# Revit family: BuzziPebl - Ceiling Hosted3
name_source: partatom
category: Furniture
revit_build: Autodesk Revit 2018 (Build: 20170223_1515(x64)
units: mm (PartAtom-declared; Revit-internal decimal feet)

## family parameters
Always vertical = Yes
Cut with Voids When Loaded = No
Host = Ceiling
OmniClass Number = 23.80.70.11
OmniClass Title = Luminaries for Internal Lighting
Room Calculation Point = No
Shared = No

## types (8) — shared parameters
Manufacturer = BuzziSpace Studio
URL = https://www.buzzi.space

## per-type parameters (varying)
| type | Cables | Diameter | Pebl Visibility |
| BuzziPebl One Medium | No | 2' - 6 25/32" | 0 |
| BuzziPebl One Large | No | 3' - 9 9/32" | 0 |
| BuzziPebl Two Large | No | 3' - 9 9/32" | 2 |
| BuzziPebl Two Medium | No | 2' - 6 25/32" | 1 |
| BuzziPebl One Medium Suspended | Yes | 2' - 6 25/32" | 0 |
| BuzziPebl One Large Suspended | Yes | 3' - 9 9/32" | 0 |
| BuzziPebl Two Large Suspended | Yes | 3' - 9 9/32" | 2 |
| BuzziPebl Two Medium Suspended | Yes | 2' - 6 25/32" | 1 |

note: column(s) folded — value = type name in every type: Model

## geometry (parser evidence)
native form markers: Sweep x7
no freeform markers — native parametric forms only
